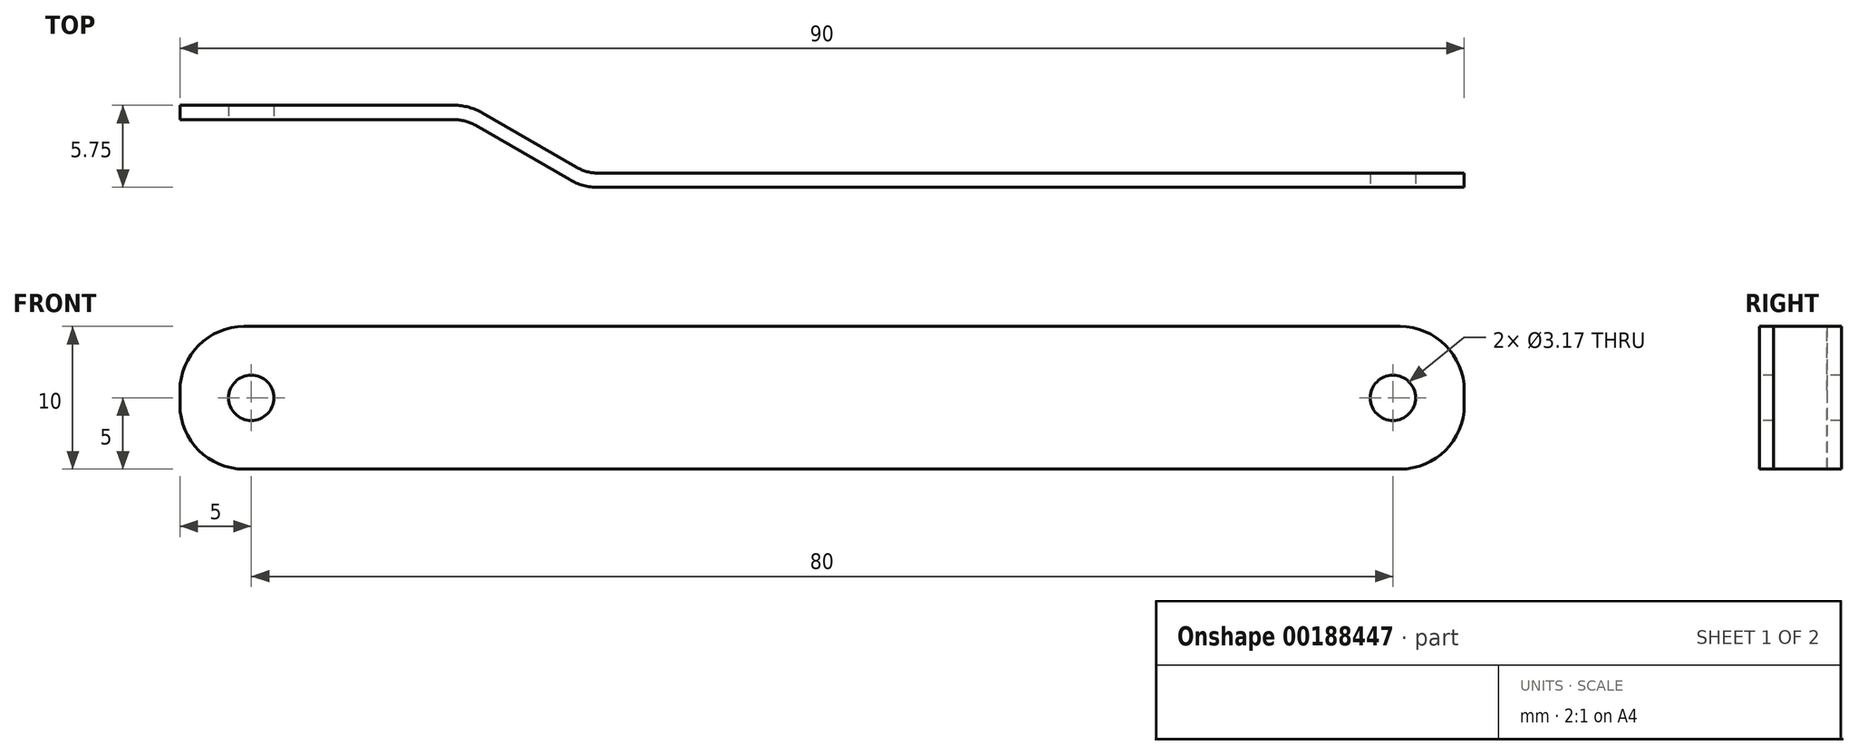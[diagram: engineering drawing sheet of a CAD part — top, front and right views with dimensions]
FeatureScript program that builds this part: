
annotation { "Feature Type Name" : "Feature", "Feature Type Description" : "" }
export const myFeature = defineFeature(function(context is Context, id is Id, definition is map)
    precondition{}
    {
        {
            var Q0;
            Q0=qCreatedBy(makeId("Top.planeOp"),FACE);
            var sketch = newSketch(context, id + "F0", { "sketchPlane" : qUnion([Q0])});
            skLineSegment(sketch, "E0", {"start": v(-69.02, 0) * mm, "end": v(67.73, 0) * mm, "construction": true});
            skLineSegment(sketch, "E1", {"start": v(-5, 11) * mm, "end": v(14.2, 11) * mm});
            skLineSegment(sketch, "E2", {"start": v(15.7, 10.6) * mm, "end": v(22.3, 6.79) * mm});
            skLineSegment(sketch, "E3", {"start": v(24.3, 6.25) * mm, "end": v(85, 6.25) * mm});
            skLineSegment(sketch, "E4.0", {"start": v(24.3, 7.25) * mm, "end": v(85, 7.25) * mm});
            skLineSegment(sketch, "E4.1", {"start": v(16.2, 11.46) * mm, "end": v(22.8, 7.65) * mm});
            skLineSegment(sketch, "E4.2", {"start": v(-5, 12) * mm, "end": v(14.2, 12) * mm});
            skLineSegment(sketch, "E5", {"start": v(-5, 11) * mm, "end": v(-5, 12) * mm});
            skLineSegment(sketch, "E6", {"start": v(85, 6.25) * mm, "end": v(85, 7.25) * mm});
            skLineSegment(sketch, "E7", {"start": v(0, 21.54) * mm, "end": v(0, 11.72) * mm, "construction": true});
            skLineSegment(sketch, "E8", {"start": v(80, 14.11) * mm, "end": v(80, 8.75) * mm, "construction": true});
            skPoint(sketch, "E9.visualSharp", {"position": v(15, 11) * mm});
            skArc(sketch, "E9.filletArc", {"start": v(15.7, 10.6) * mm, "mid": v(14.97, 10.9) * mm, "end": v(14.2, 11) * mm});
            skPoint(sketch, "E10.visualSharp", {"position": v(15.27, 12) * mm});
            skArc(sketch, "E10.filletArc", {"start": v(16.2, 11.46) * mm, "mid": v(15.23, 11.86) * mm, "end": v(14.2, 12) * mm});
            skPoint(sketch, "E11.visualSharp", {"position": v(23.5, 7.25) * mm});
            skArc(sketch, "E11.filletArc", {"start": v(22.8, 7.65) * mm, "mid": v(23.52, 7.35) * mm, "end": v(24.3, 7.25) * mm});
            skPoint(sketch, "E12.visualSharp", {"position": v(23.23, 6.25) * mm});
            skArc(sketch, "E12.filletArc", {"start": v(22.3, 6.79) * mm, "mid": v(23.26, 6.39) * mm, "end": v(24.3, 6.25) * mm});
            skSolve(sketch);
        }
        {
            var Q0;
            Q0=qSketchRegion(id+"F0",true);
            extrude(context, id + "F1", {"entities" : qUnion([Q0]), "endBound" : BoundingType.SYMMETRIC, "depth" : 10 * mm, "offsetDistance" : 25 * mm});
        }
        {
            var Q0;
            Q0=qCreatedBy(makeId("Front.planeOp"),FACE);
            var sketch = newSketch(context, id + "F2", { "sketchPlane" : qUnion([Q0])});
            skPoint(sketch, "E13", {"position": v(0, 0) * mm});
            skPoint(sketch, "E14", {"position": v(80, 0) * mm});
            skSolve(sketch);
        }
        {
            var Q0;
            Q0=sQuery(id+"F2.wireOp",VERTEX,"E13");
            var Q1;
            Q1=sQuery(id+"F2.wireOp",VERTEX,"E14");
            var Q2;
            Q2=makeQuery(id+"F1.opExtrude","SWEPT_BODY",BODY,{"disambiguationData":[OSD([sQuery(id+"F0.wireOp",EDGE,"E1"),sQuery(id+"F0.wireOp",EDGE,"E2"),sQuery(id+"F0.wireOp",EDGE,"E3"),sQuery(id+"F0.wireOp",EDGE,"E4.0"),sQuery(id+"F0.wireOp",EDGE,"E4.1"),sQuery(id+"F0.wireOp",EDGE,"E4.2"),sQuery(id+"F0.wireOp",EDGE,"E5"),sQuery(id+"F0.wireOp",EDGE,"E6"),sQuery(id+"F0.wireOp",EDGE,"E9.filletArc"),sQuery(id+"F0.wireOp",EDGE,"E10.filletArc"),sQuery(id+"F0.wireOp",EDGE,"E11.filletArc"),sQuery(id+"F0.wireOp",EDGE,"E12.filletArc")])]});
            hole(context, id + "F3", {"style" : HoleStyle.SIMPLE, "endStyle" : HoleEndStyle.THROUGH, "holeDiameter" : 3.17 * mm, "majorDiameter" : 5 * mm, "isTappedThrough" : true, "tappedDepth" : 12 * mm, "tapClearance" : 3, "startFromSketch" : true, "locations" : qUnion([Q0, Q1]), "scope" : qUnion([Q2])});
        }
        {
            var Q0;
            Q0=makeQuery(id+"F1.opExtrude","CAP_EDGE",EDGE,{"disambiguationData":[OSD([sQuery(id+"F0.wireOp",EDGE,"E6")])],"isStart":false});
            var Q1;
            Q1=makeQuery(id+"F1.opExtrude","CAP_EDGE",EDGE,{"disambiguationData":[OSD([sQuery(id+"F0.wireOp",EDGE,"E6")])],"isStart":true});
            var Q2;
            Q2=makeQuery(id+"F1.opExtrude","CAP_EDGE",EDGE,{"disambiguationData":[OSD([sQuery(id+"F0.wireOp",EDGE,"E5")])],"isStart":false});
            var Q3;
            Q3=makeQuery(id+"F1.opExtrude","CAP_EDGE",EDGE,{"disambiguationData":[OSD([sQuery(id+"F0.wireOp",EDGE,"E5")])],"isStart":true});
            fillet(context, id + "F4", {"entities" : qUnion([Q0, Q1, Q2, Q3]), "radius" : 4.5 * mm, "tangentPropagation" : true, "allowEdgeOverflow" : false});
        }
    });
